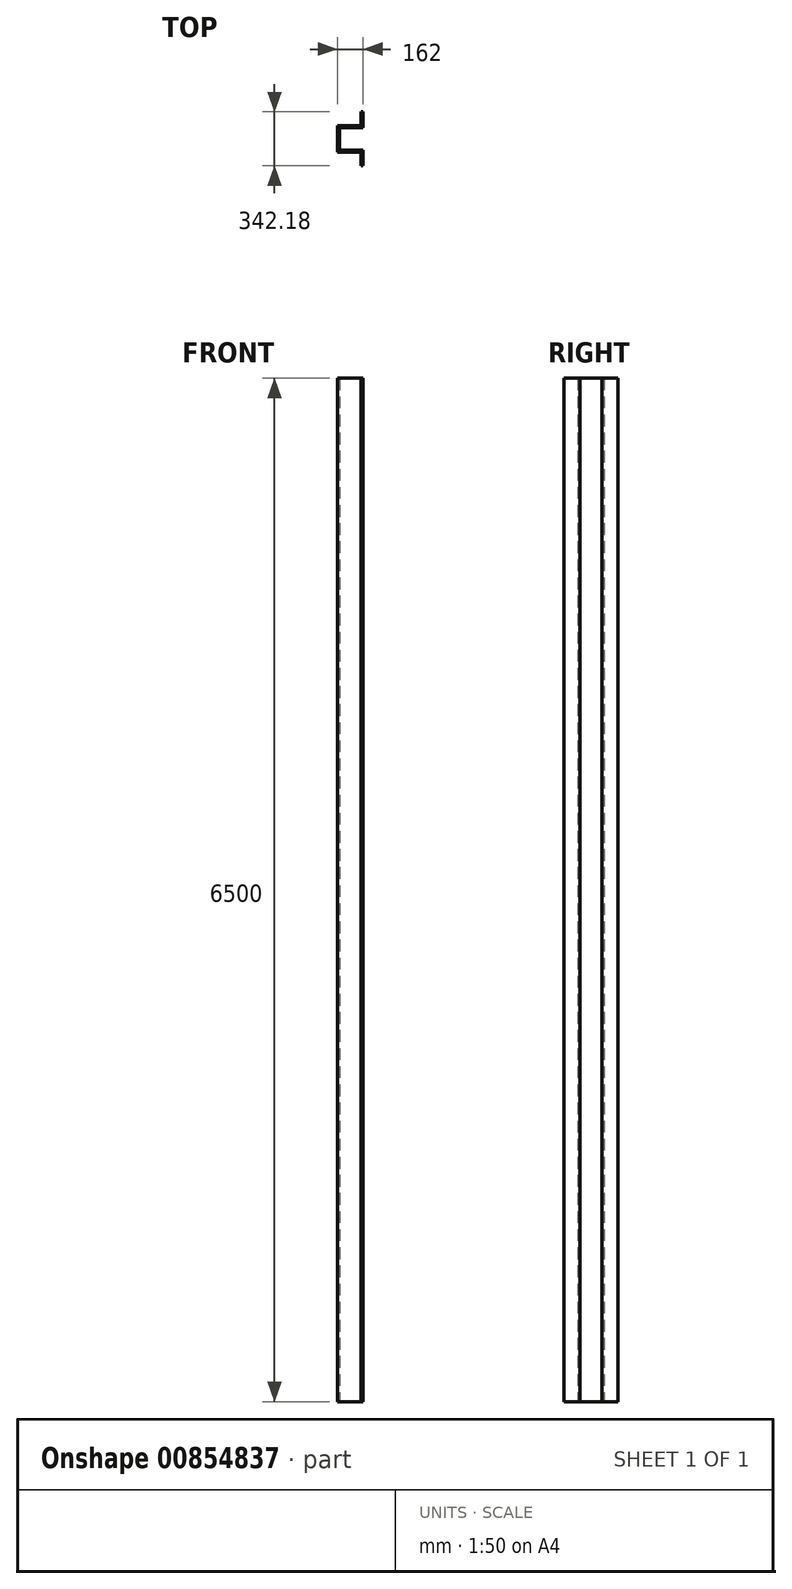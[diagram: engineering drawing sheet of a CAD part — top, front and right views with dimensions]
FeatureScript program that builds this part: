
annotation { "Feature Type Name" : "Feature", "Feature Type Description" : "" }
export const myFeature = defineFeature(function(context is Context, id is Id, definition is map)
    precondition{}
    {
        {
            var Q0;
            Q0=qCreatedBy(makeId("Top.planeOp"),FACE);
            var sketch = newSketch(context, id + "F0", { "sketchPlane" : qUnion([Q0])});
            skLineSegment(sketch, "E0", {"start": v(0, 0) * mm, "end": v(0, 100) * mm});
            skLineSegment(sketch, "E1", {"start": v(0, 100) * mm, "end": v(-150, 100) * mm});
            skLineSegment(sketch, "E2", {"start": v(-150, 100) * mm, "end": v(-150, 242.18) * mm});
            skLineSegment(sketch, "E3", {"start": v(-150, 242.18) * mm, "end": v(0, 242.18) * mm});
            skLineSegment(sketch, "E4", {"start": v(0, 242.18) * mm, "end": v(0, 342.18) * mm});
            skLineSegment(sketch, "E5", {"start": v(0, 0) * mm, "end": v(-12, 0) * mm});
            skLineSegment(sketch, "E6", {"start": v(-12, 0) * mm, "end": v(-12, 88) * mm});
            skLineSegment(sketch, "E7", {"start": v(-12, 88) * mm, "end": v(-162, 88) * mm});
            skLineSegment(sketch, "E8", {"start": v(-162, 88) * mm, "end": v(-162, 254.18) * mm});
            skLineSegment(sketch, "E9", {"start": v(-162, 254.18) * mm, "end": v(-12, 254.18) * mm});
            skLineSegment(sketch, "E10", {"start": v(-12, 254.18) * mm, "end": v(-12, 342.18) * mm});
            skLineSegment(sketch, "E11", {"start": v(-12, 342.18) * mm, "end": v(0, 342.18) * mm});
            skSolve(sketch);
        }
        {
            var Q0;
            Q0=makeQuery(id+"F0.imprint","IMPRINT",FACE,{"disambiguationData":[TD([[makeQuery(id+"F0.imprint","IMPRINT",EDGE,{"derivedFrom":sQuery(id+"F0.wireOp",EDGE,"E0")}),1.0]])]});
            extrude(context, id + "F1", {"entities" : qUnion([Q0]), "depth" : 6500 * mm, "offsetDistance" : 25 * mm});
        }
    });
